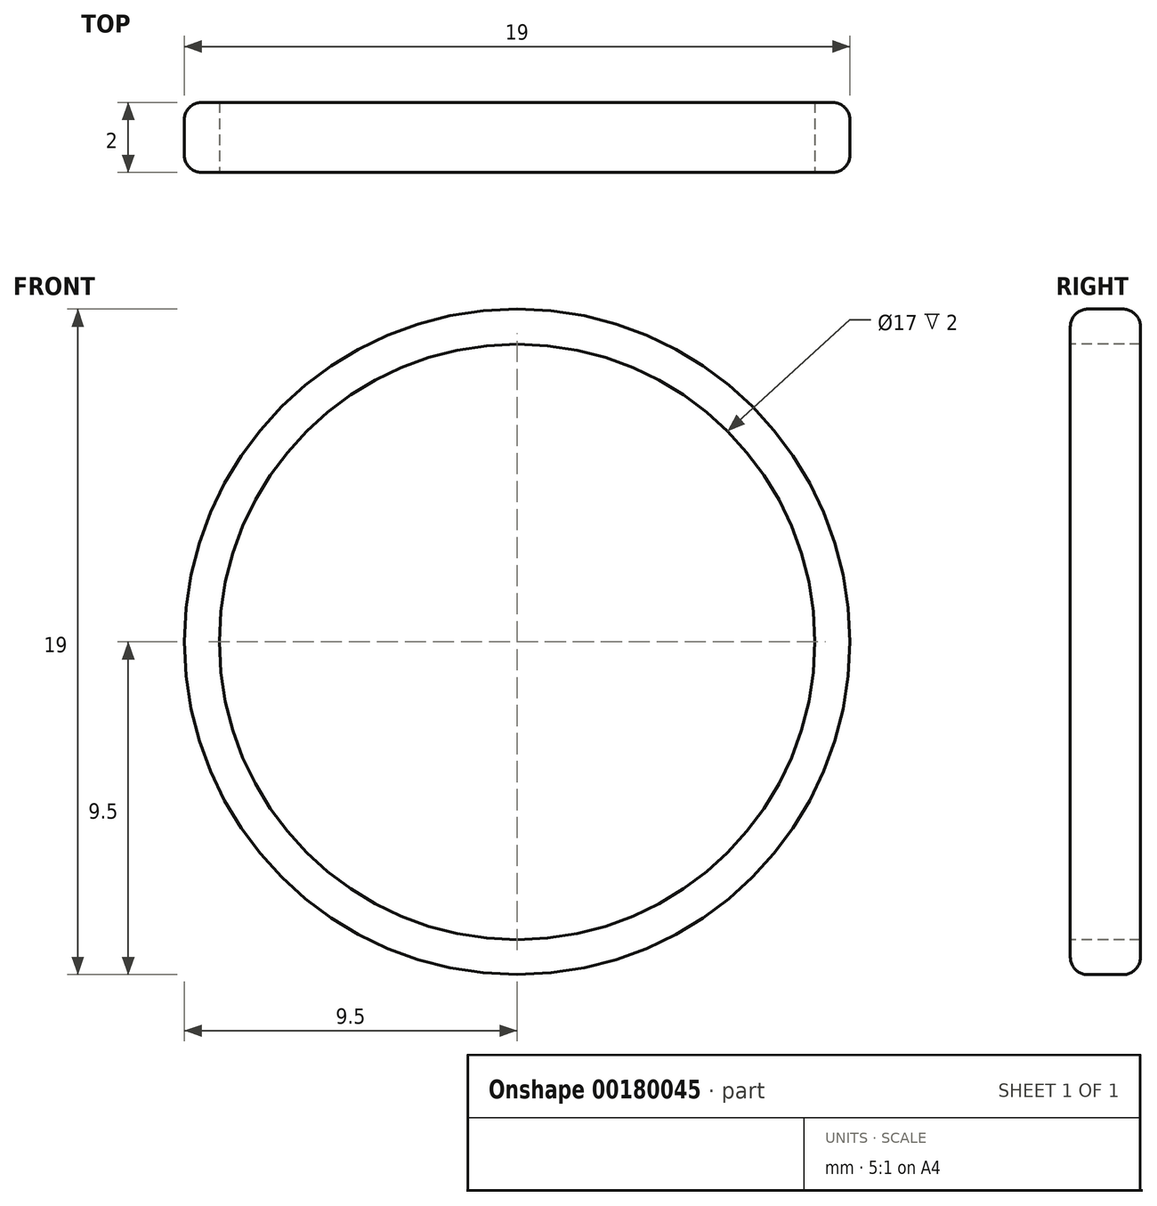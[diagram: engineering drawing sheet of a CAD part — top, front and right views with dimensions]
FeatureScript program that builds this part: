
annotation { "Feature Type Name" : "Feature", "Feature Type Description" : "" }
export const myFeature = defineFeature(function(context is Context, id is Id, definition is map)
    precondition{}
    {
        {
            var Q0;
            Q0=qCreatedBy(makeId("Front.planeOp"),FACE);
            var sketch = newSketch(context, id + "F0", { "sketchPlane" : qUnion([Q0])});
            skCircle(sketch, "E0", {"center": v(0, 0) * mm, "radius": 9.5 * mm});
            skSolve(sketch);
        }
        {
            var Q0;
            Q0=makeQuery(id+"F0.imprint","IMPRINT",FACE,{"disambiguationData":[TD([[makeQuery(id+"F0.imprint","IMPRINT",EDGE,{"derivedFrom":sQuery(id+"F0.wireOp",EDGE,"E0")}),1.0]])]});
            extrude(context, id + "F1", {"entities" : qUnion([Q0]), "depth" : 2 * mm});
        }
        {
            var Q0;
            Q0=makeQuery(id+"F1.opExtrude","CAP_FACE",FACE,{"disambiguationData":[OSD([sQuery(id+"F0.wireOp",EDGE,"E0")])],"isStart":false});
            var sketch = newSketch(context, id + "F2", { "sketchPlane" : qUnion([Q0])});
            skCircle(sketch, "E1", {"center": v(0, 0) * mm, "radius": 8.5 * mm});
            skSolve(sketch);
        }
        {
            var Q0;
            Q0=makeQuery(id+"F2.imprint","IMPRINT",FACE,{"disambiguationData":[TD([[makeQuery(id+"F2.imprint","IMPRINT",EDGE,{"derivedFrom":sQuery(id+"F2.wireOp",EDGE,"E1")}),1.0]])]});
            extrude(context, id + "F3", {"entities" : qUnion([Q0]), "operationType" : NewBodyOperationType.REMOVE, "endBound" : BoundingType.THROUGH_ALL, "oppositeDirection" : true, "depth" : 25 * mm});
        }
        {
            var Q0;
            Q0=makeQuery(id+"F1.opExtrude","CAP_EDGE",EDGE,{"disambiguationData":[OSD([sQuery(id+"F0.wireOp",EDGE,"E0")])],"isStart":false});
            var Q1;
            Q1=makeQuery(id+"F1.opExtrude","CAP_EDGE",EDGE,{"disambiguationData":[OSD([sQuery(id+"F0.wireOp",EDGE,"E0")])],"isStart":true});
            fillet(context, id + "F4", {"entities" : qUnion([Q0, Q1]), "radius" : 0.5 * mm, "tangentPropagation" : true, "allowEdgeOverflow" : false});
        }
    });
